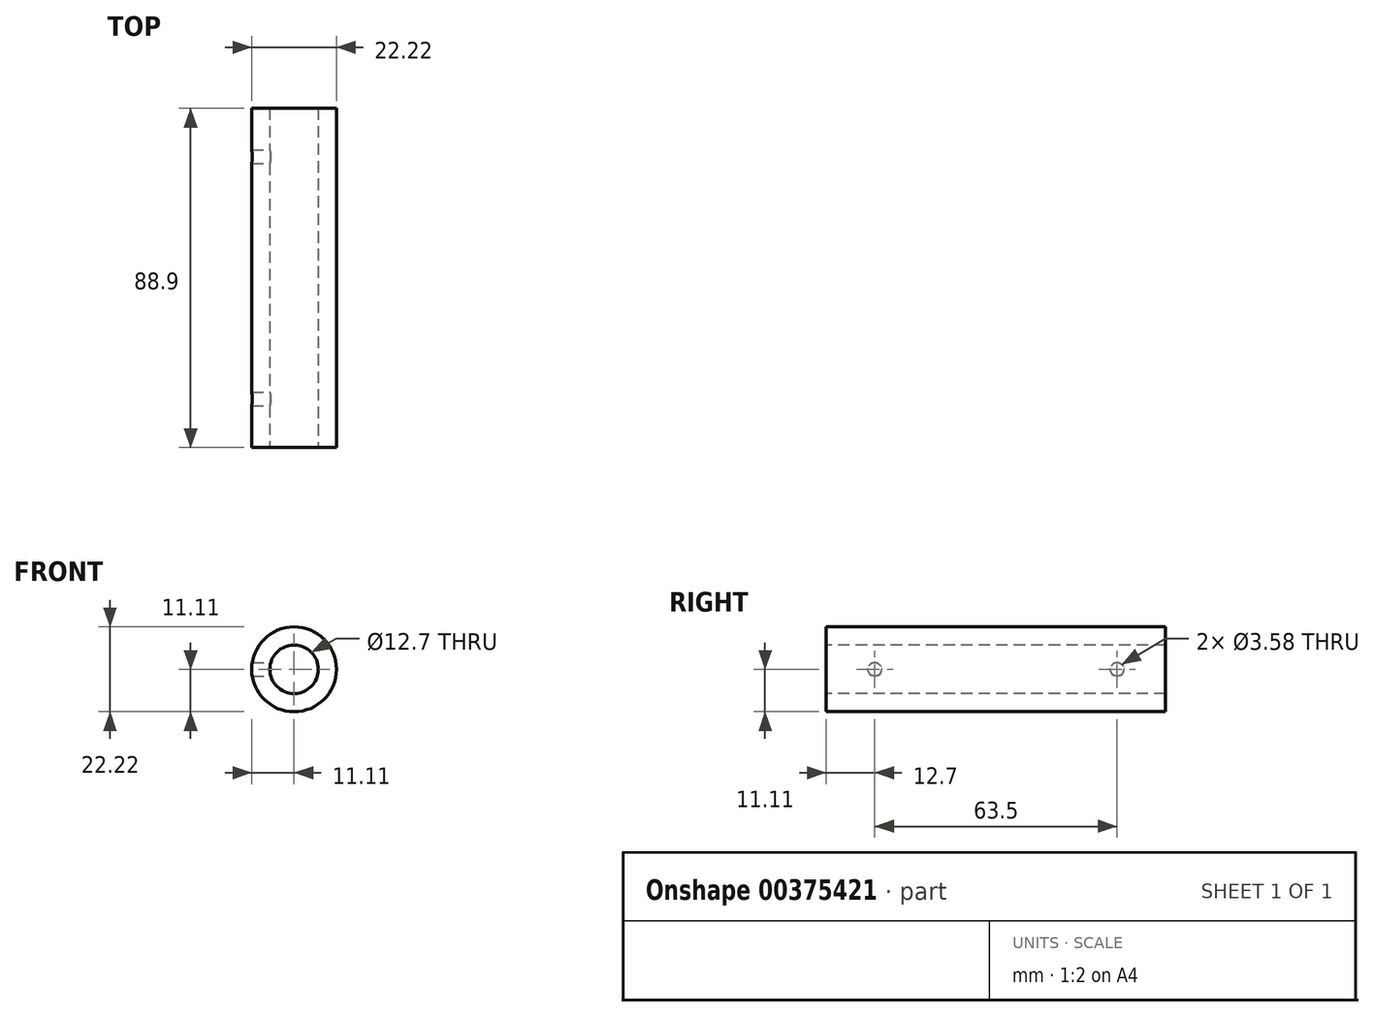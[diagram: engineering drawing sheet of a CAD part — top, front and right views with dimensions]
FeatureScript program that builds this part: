
annotation { "Feature Type Name" : "Feature", "Feature Type Description" : "" }
export const myFeature = defineFeature(function(context is Context, id is Id, definition is map)
    precondition{}
    {
        {
            var Q0;
            Q0=qCreatedBy(makeId("Front.planeOp"),FACE);
            var sketch = newSketch(context, id + "F0", { "sketchPlane" : qUnion([Q0])});
            skCircle(sketch, "E0", {"center": v(0, 0) * mm, "radius": 11.11 * mm});
            skSolve(sketch);
        }
        {
            var Q0;
            Q0=qSketchRegion(id+"F0",true);
            extrude(context, id + "F1", {"entities" : qUnion([Q0]), "depth" : 88.9 * mm, "symmetric" : true});
        }
        {
            var Q0;
            Q0=makeQuery(id+"F1.opExtrude","CAP_FACE",FACE,{"disambiguationData":[OSD([sQuery(id+"F0.wireOp",EDGE,"E0")])],"isStart":false});
            var sketch = newSketch(context, id + "F2", { "sketchPlane" : qUnion([Q0])});
            skCircle(sketch, "E1", {"center": v(0, 0) * mm, "radius": 6.35 * mm});
            skSolve(sketch);
        }
        {
            var Q0;
            Q0=qSketchRegion(id+"F2",true);
            extrude(context, id + "F3", {"entities" : qUnion([Q0]), "operationType" : NewBodyOperationType.REMOVE, "oppositeDirection" : true, "depth" : 88.9 * mm});
        }
        {
            var Q0;
            Q0=qCreatedBy(makeId("Right.planeOp"),FACE);
            var sketch = newSketch(context, id + "F4", { "sketchPlane" : qUnion([Q0])});
            skCircle(sketch, "E2", {"center": v(-31.75, 0) * mm, "radius": 1.8 * mm});
            skSolve(sketch);
        }
        {
            var Q0;
            Q0=qSketchRegion(id+"F4",true);
            extrude(context, id + "F5", {"entities" : qUnion([Q0]), "operationType" : NewBodyOperationType.REMOVE, "endBound" : BoundingType.THROUGH_ALL, "oppositeDirection" : true, "depth" : 12.7 * mm});
        }
        {
            var Q0;
            Q0=qCreatedBy(makeId("Right.planeOp"),FACE);
            var sketch = newSketch(context, id + "F6", { "sketchPlane" : qUnion([Q0])});
            skCircle(sketch, "E3", {"center": v(31.75, 0) * mm, "radius": 1.8 * mm});
            skSolve(sketch);
        }
        {
            var Q0;
            Q0=qSketchRegion(id+"F6",true);
            extrude(context, id + "F7", {"entities" : qUnion([Q0]), "operationType" : NewBodyOperationType.REMOVE, "endBound" : BoundingType.THROUGH_ALL, "oppositeDirection" : true, "depth" : 22.22 * mm});
        }
    });
